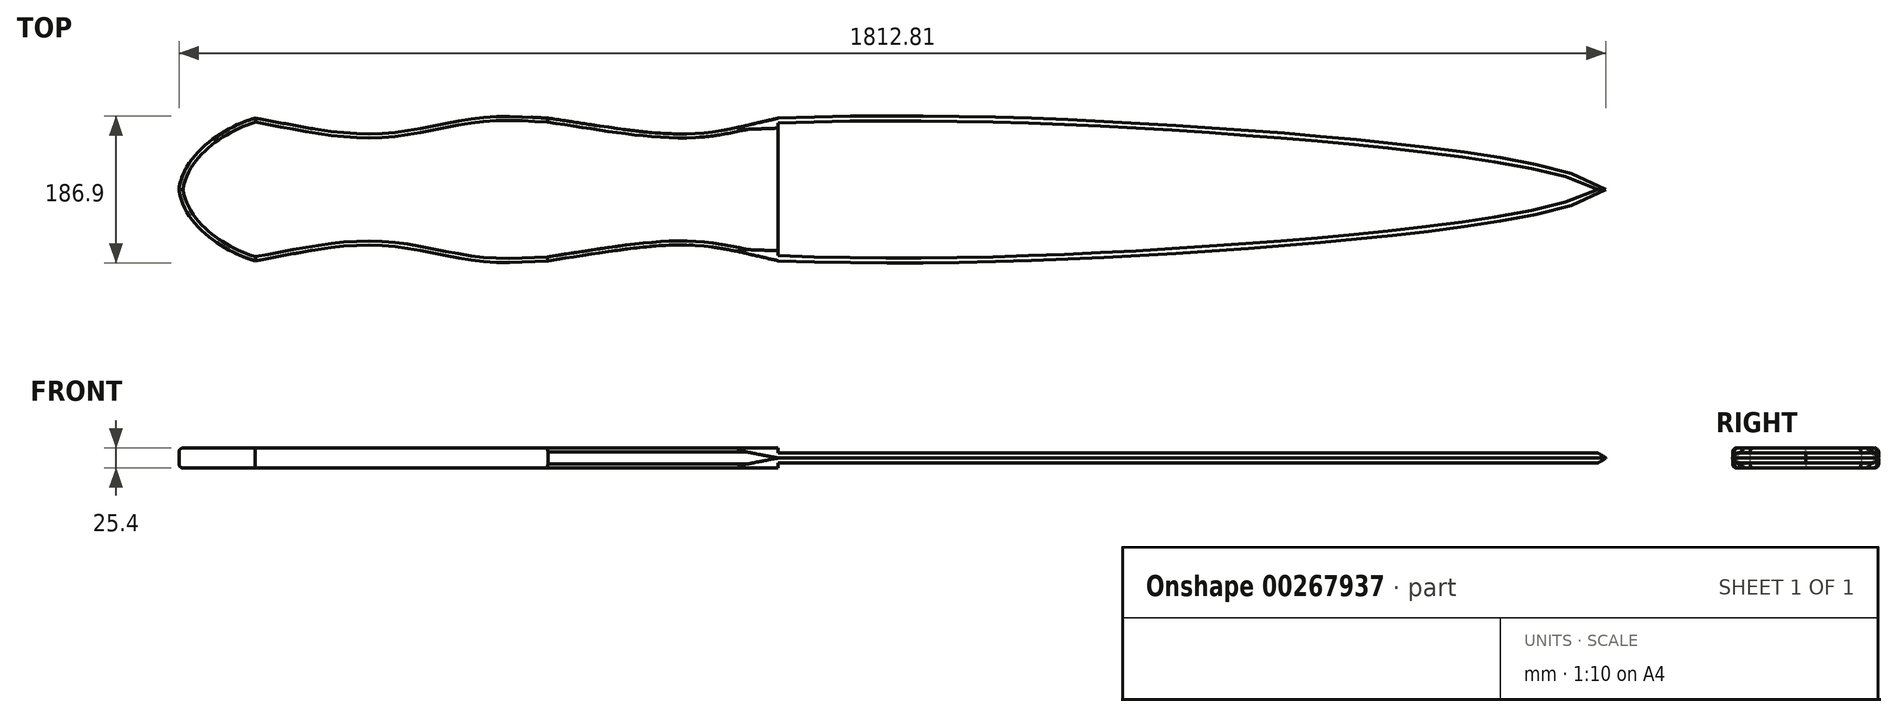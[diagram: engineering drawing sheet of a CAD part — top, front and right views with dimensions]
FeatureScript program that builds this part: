
annotation { "Feature Type Name" : "Feature", "Feature Type Description" : "" }
export const myFeature = defineFeature(function(context is Context, id is Id, definition is map)
    precondition{}
    {
        {
            var Q0;
            Q0=qCreatedBy(makeId("Top.planeOp"),FACE);
            var sketch = newSketch(context, id + "F0", { "sketchPlane" : qUnion([Q0])});
            skLineSegment(sketch, "E0", {"start": v(0, 0) * mm, "end": v(-761.19, 0) * mm, "construction": true});
            skLineSegment(sketch, "E1", {"start": v(0, 0) * mm, "end": v(1051.62, 0) * mm, "construction": true});
            skFitSpline(sketch, "E2", {"points": [v(1051.62, 0) * mm, v(536.57, 79.22) * mm, v(0, 90.57) * mm], "startDerivative": vector(-256.52, 239.94) * mm, "endDerivative": vector(-944.73, -35.12) * mm});
            skFitSpline(sketch, "E3", {"points": [v(0, 90.57) * mm, v(-113.13, 70.67) * mm, v(-292.65, 90.57) * mm], "startDerivative": vector(-240.28, -51.47) * mm, "endDerivative": vector(-341.2, 47.72) * mm});
            skFitSpline(sketch, "E4", {"points": [v(-292.65, 90.57) * mm, v(-382.4, 90.57) * mm, v(-510.64, 70.67) * mm, v(-664.2, 90.57) * mm], "startDerivative": vector(-301.9, 16.92) * mm, "endDerivative": vector(-412.5, 72.96) * mm});
            skFitSpline(sketch, "E5", {"points": [v(-664.2, 90.57) * mm, v(-761.19, 0) * mm], "startDerivative": vector(-124.97, -34.22) * mm, "endDerivative": vector(-13.74, -129.69) * mm});
            skLineSegment(sketch, "E6", {"start": v(0, 90.57) * mm, "end": v(0, 0) * mm});
            skFitSpline(sketch, "E7.MirrorCS", {"points": [v(0, -90.57) * mm, v(-113.13, -70.67) * mm, v(-292.65, -90.57) * mm], "startDerivative": vector(-240.28, 51.47) * mm, "endDerivative": vector(-341.2, -47.72) * mm});
            skFitSpline(sketch, "E8.MirrorCS", {"points": [v(-292.65, -90.57) * mm, v(-382.4, -90.57) * mm, v(-510.64, -70.67) * mm, v(-664.2, -90.57) * mm], "startDerivative": vector(-301.9, -16.92) * mm, "endDerivative": vector(-412.5, -72.96) * mm});
            skFitSpline(sketch, "E9.MirrorCS", {"points": [v(-664.2, -90.57) * mm, v(-761.19, 0) * mm], "startDerivative": vector(-124.97, 34.22) * mm, "endDerivative": vector(-13.74, 129.69) * mm});
            skLineSegment(sketch, "E10.MirrorCS", {"start": v(0, -90.57) * mm, "end": v(0, 0) * mm});
            skFitSpline(sketch, "E11.MirrorCS", {"points": [v(1051.62, 0) * mm, v(536.57, -79.22) * mm, v(0, -90.57) * mm], "startDerivative": vector(-256.52, -239.94) * mm, "endDerivative": vector(-944.73, 35.12) * mm});
            skSolve(sketch);
        }
        {
            var Q0;
            Q0=makeQuery(id+"F0.imprint","IMPRINT",FACE,{"disambiguationData":[TD([[makeQuery(id+"F0.imprint","IMPRINT",EDGE,{"derivedFrom":sQuery(id+"F0.wireOp",EDGE,"E3")}),1.0]])]});
            extrude(context, id + "F1", {"entities" : qUnion([Q0]), "depth" : 12.7 * mm, "hasSecondDirection" : true, "secondDirectionOppositeDirection" : true, "secondDirectionDepth" : 12.7 * mm});
        }
        {
            var Q0;
            Q0=makeQuery(id+"F0.imprint","IMPRINT",FACE,{"disambiguationData":[TD([[makeQuery(id+"F0.imprint","IMPRINT",EDGE,{"derivedFrom":sQuery(id+"F0.wireOp",EDGE,"E2")}),1.0]])]});
            extrude(context, id + "F2", {"entities" : qUnion([Q0]), "operationType" : NewBodyOperationType.ADD, "depth" : 6.35 * mm, "hasSecondDirection" : true, "secondDirectionOppositeDirection" : true, "secondDirectionDepth" : 6.35 * mm});
        }
        {
            var Q0;
            Q0=makeQuery(id+"F2.opExtrude","CAP_EDGE",EDGE,{"disambiguationData":[OSD([sQuery(id+"F0.wireOp",EDGE,"E2")])],"isStart":false});
            var Q1;
            Q1=makeQuery(id+"F2.opExtrude","CAP_EDGE",EDGE,{"disambiguationData":[OSD([sQuery(id+"F0.wireOp",EDGE,"E11.MirrorCS")])],"isStart":false});
            var Q2;
            Q2=makeQuery(id+"F2.opExtrude","CAP_EDGE",EDGE,{"disambiguationData":[OSD([sQuery(id+"F0.wireOp",EDGE,"E11.MirrorCS")])],"isStart":true});
            var Q3;
            Q3=makeQuery(id+"F2.opExtrude","CAP_EDGE",EDGE,{"disambiguationData":[OSD([sQuery(id+"F0.wireOp",EDGE,"E2")])],"isStart":true});
            chamfer(context, id + "F3", {"entities" : qUnion([Q0, Q1, Q2, Q3]), "chamferType" : ChamferType.OFFSET_ANGLE, "width" : 6.35 * mm, "oppositeDirection" : false, "angle" : 45 * degree, "tangentPropagation" : true});
        }
        {
            var Q0;
            Q0=makeQuery(id+"F1.opExtrude","CAP_EDGE",EDGE,{"disambiguationData":[OSD([sQuery(id+"F0.wireOp",EDGE,"E4")])],"isStart":false});
            var Q1;
            Q1=makeQuery(id+"F1.opExtrude","CAP_EDGE",EDGE,{"disambiguationData":[OSD([sQuery(id+"F0.wireOp",EDGE,"E5")])],"isStart":false});
            var Q2;
            Q2=makeQuery(id+"F1.opExtrude","CAP_EDGE",EDGE,{"disambiguationData":[OSD([sQuery(id+"F0.wireOp",EDGE,"E9.MirrorCS")])],"isStart":false});
            var Q3;
            Q3=makeQuery(id+"F1.opExtrude","CAP_EDGE",EDGE,{"disambiguationData":[OSD([sQuery(id+"F0.wireOp",EDGE,"E8.MirrorCS")])],"isStart":false});
            var Q4;
            Q4=makeQuery(id+"F1.opExtrude","CAP_EDGE",EDGE,{"disambiguationData":[OSD([sQuery(id+"F0.wireOp",EDGE,"E7.MirrorCS")])],"isStart":false});
            var Q5;
            Q5=makeQuery(id+"F1.opExtrude","CAP_EDGE",EDGE,{"disambiguationData":[OSD([sQuery(id+"F0.wireOp",EDGE,"E3")])],"isStart":false});
            var Q6;
            Q6=makeQuery(id+"F1.opExtrude","CAP_EDGE",EDGE,{"disambiguationData":[OSD([sQuery(id+"F0.wireOp",EDGE,"E7.MirrorCS")])],"isStart":true});
            var Q7;
            Q7=makeQuery(id+"F1.opExtrude","CAP_EDGE",EDGE,{"disambiguationData":[OSD([sQuery(id+"F0.wireOp",EDGE,"E8.MirrorCS")])],"isStart":true});
            var Q8;
            Q8=makeQuery(id+"F1.opExtrude","CAP_EDGE",EDGE,{"disambiguationData":[OSD([sQuery(id+"F0.wireOp",EDGE,"E9.MirrorCS")])],"isStart":true});
            var Q9;
            Q9=makeQuery(id+"F1.opExtrude","CAP_EDGE",EDGE,{"disambiguationData":[OSD([sQuery(id+"F0.wireOp",EDGE,"E3")])],"isStart":true});
            var Q10;
            Q10=makeQuery(id+"F1.opExtrude","CAP_EDGE",EDGE,{"disambiguationData":[OSD([sQuery(id+"F0.wireOp",EDGE,"E4")])],"isStart":true});
            var Q11;
            Q11=makeQuery(id+"F1.opExtrude","CAP_EDGE",EDGE,{"disambiguationData":[OSD([sQuery(id+"F0.wireOp",EDGE,"E5")])],"isStart":true});
            fillet(context, id + "F4", {"entities" : qUnion([Q0, Q1, Q2, Q3, Q4, Q5, Q6, Q7, Q8, Q9, Q10, Q11]), "radius" : 5.08 * mm, "tangentPropagation" : true, "allowEdgeOverflow" : false});
        }
    });
